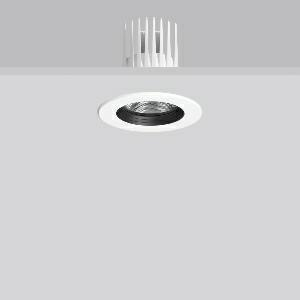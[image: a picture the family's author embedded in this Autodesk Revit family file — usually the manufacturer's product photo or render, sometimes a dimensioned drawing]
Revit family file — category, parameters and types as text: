
# Revit family: heledon_mini_e_901748_002_3_76_7523
name_source: partatom
category: Lighting Fixtures
units: mm (PartAtom-declared; Revit-internal decimal feet)

## family parameters
Cut with Voids When Loaded = No
Host = Face
Light Source = No
Part Type = Normal
Room Calculation Point = No
Round Connector Dimension = Use Diameter
Shared = No

## types (1)
- HELEDON mini E (1 x LED Modul 935, 3700 lm, 3500)
    Apparent Load = 29 VA
    Approval mark = CE
    CIE Flux Codes = 100 100 100 100 100
    Color Rendering = 92
    Color Temperature = 3500
    Default Elevation = 1800 mm
    Description = Series: HELEDON mini
Round recessed downlight. Housing: die-cast aluminium, powder-coated. Black plastic ring and recessed LED to prevent glare from the side. Optical assembly with reflector made of MIRO-Silver with 98% total light reflection for outstanding efficiency - can be changed without tools. Best colour rendering index Ra>90. Suitable for Recessed ceiling mounting. Installation without tools thanks to spring fastening system. Including separate LED converter with connecting cable 600 mm.High quality converter without flickering and stroboscopic effect. Through-wiring box (5 pole) available as accessory. The following accessories can be mounted without use of tools: interchangeable lenses, decorative glasses, honeycomb louvre, clear and frosted diffusers, white interchangeable plastic ring. 
Colour: traffic white, matt (RAL 9016)
Diameter: 124 mm
Height: 3 mm
Cut-out diameter: 114 mm
Recess height: 170 mm
Luminaire: recess height: 120 mm
Lamp: LED
Socket: without socket
Colour temperature: 3500K
Colour rendering index (CRI): 92
System power: 29 W
Rated luminous flux: 3700 lm
Luminous efficiency: 128 lm/W
Control gear: Converter, dimmable, DALI
Protection class: II
Type of protection: IP 20
    Height = 0 mm  [stored 0 ft]
    Lamp = 1 x LED Modul 935
    Lamp Light Flux = 3700 lm
    Lamp count = 1
    Length = 124 mm  [stored 0.406824 ft]
    Lifetime = 50000 h
    Luminous efficacy = 128 lm/W
    Manufacturer = RZB
    ModVariant = No
    Model = 901748.002.3.76
    Mounting Place = Ceiling
    Mounting Type = Recessed
    Number of Poles = 1
    OnlyDefault = Yes
    Power Factor = 1
    Product Name = HELEDON mini E
    Product group = Recessed downlights
    ProductGroupID = 402
    Protection Class = Protection class II
    Protection Degree = IP 20
    RLX_Detail_Level = 1
    RLX_Emergency_Light_Flux = 0 lm
    RLX_Emergency_Type = 0
    RLX_Emergency_Type_DB = No
    RlxData = <blob elided: 127049 chars, md5=df752785>
    Socket = socket
    Standby Power = 0 W
    System Light Flux = 3700 lm
    System Power = 29 W
    Type Comments = Product without accessories
    Type Image = 901657.002.jpg
    URL = http://relux.com
    VarID = ---
    Voltage = 230 V
    Voltage Range = 220-240 V
    Weight = 0.00 kg
    Width = 0 mm  [stored 0 ft]

note: [stored X ft] marks values corroborated as IEEE doubles in the binary element streams (Revit-internal decimal feet)

## geometry (parser evidence)
native form markers: Blend x4, Sweep x11
no freeform markers — native parametric forms only
